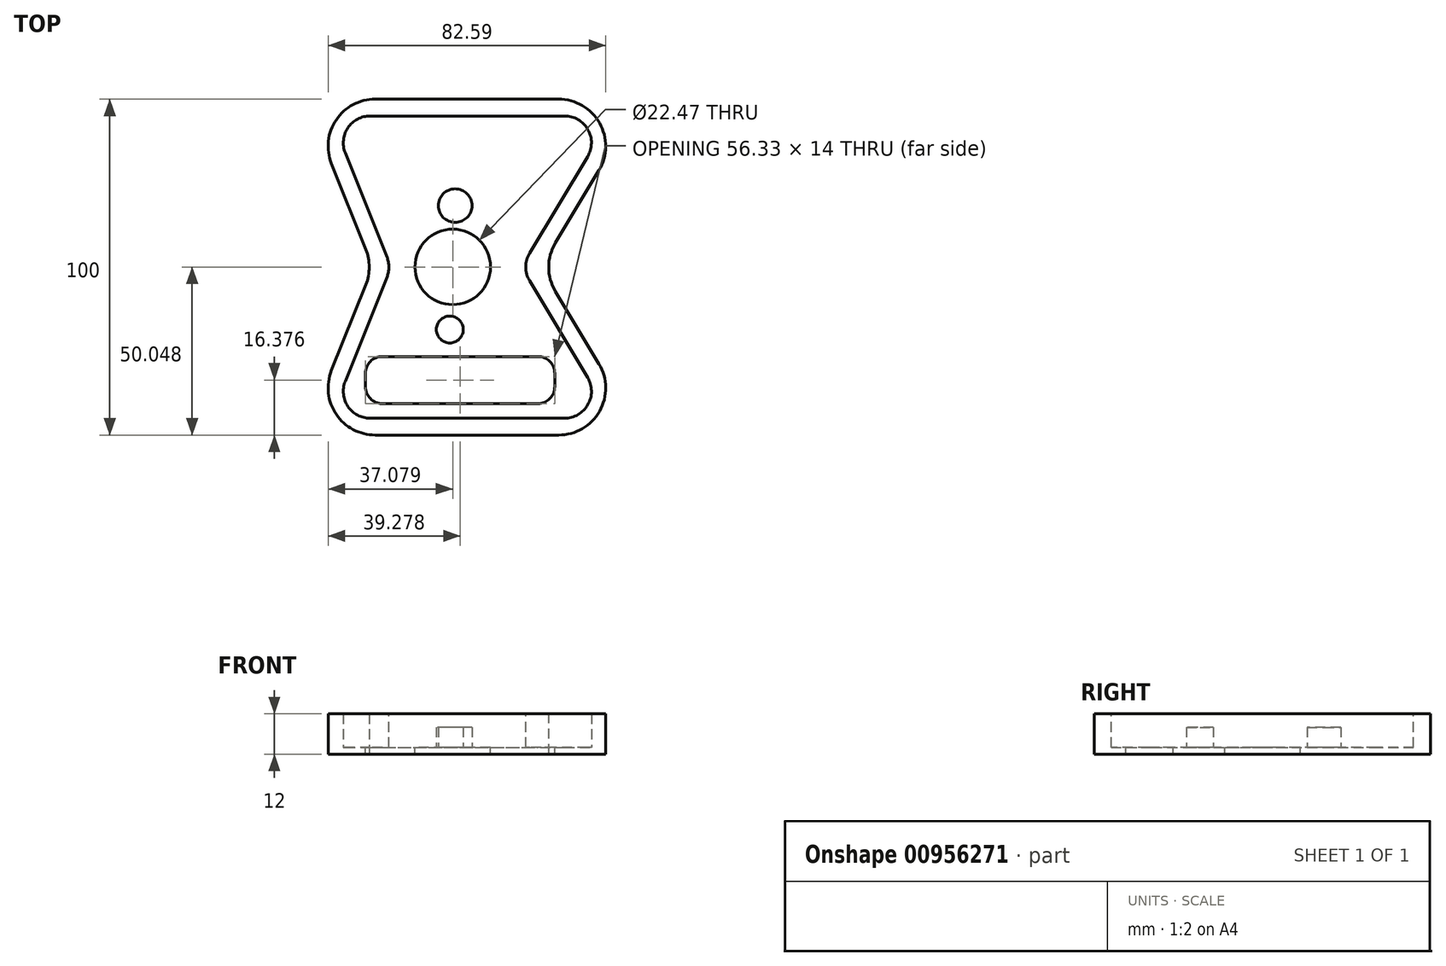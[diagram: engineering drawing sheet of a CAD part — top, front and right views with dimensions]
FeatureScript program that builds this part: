
annotation { "Feature Type Name" : "Feature", "Feature Type Description" : "" }
export const myFeature = defineFeature(function(context is Context, id is Id, definition is map)
    precondition{}
    {
        {
            var Q0;
            Q0=qCreatedBy(makeId("Top.planeOp"),FACE);
            var sketch = newSketch(context, id + "F0", { "sketchPlane" : qUnion([Q0])});
            skLineSegment(sketch, "E0.bottom", {"start": v(0, 0) * mm, "end": v(100, 0) * mm});
            skLineSegment(sketch, "E0.top", {"start": v(0, 100) * mm, "end": v(100, 100) * mm});
            skLineSegment(sketch, "E0.left", {"start": v(0, 0) * mm, "end": v(0, 100) * mm, "construction": true});
            skLineSegment(sketch, "E0.right", {"start": v(100, 0) * mm, "end": v(100, 100) * mm, "construction": true});
            skLineSegment(sketch, "E1", {"start": v(50, 0) * mm, "end": v(50, 100) * mm, "construction": true});
            skLineSegment(sketch, "E2", {"start": v(50, 50) * mm, "end": v(20, 50) * mm, "construction": true});
            skLineSegment(sketch, "E3", {"start": v(50, 50) * mm, "end": v(70, 50) * mm, "construction": true});
            skLineSegment(sketch, "E4", {"start": v(0, 100) * mm, "end": v(20, 50) * mm});
            skLineSegment(sketch, "E5", {"start": v(0, 0) * mm, "end": v(20, 50) * mm});
            skLineSegment(sketch, "E6", {"start": v(100, 0) * mm, "end": v(70, 50) * mm});
            skLineSegment(sketch, "E7", {"start": v(70, 50) * mm, "end": v(100, 100) * mm});
            skSolve(sketch);
        }
        {
            var Q0;
            Q0=makeQuery(id+"F0.imprint","IMPRINT",FACE,{"disambiguationData":[TD([[makeQuery(id+"F0.imprint","IMPRINT",EDGE,{"derivedFrom":sQuery(id+"F0.wireOp",EDGE,"E0.bottom")}),1.0]])]});
            extrude(context, id + "F1", {"entities" : qUnion([Q0]), "depth" : 12 * mm, "offsetDistance" : 25 * mm});
        }
        {
            var Q0;
            Q0=makeQuery(id+"F1.opExtrude","CAP_FACE",FACE,{"disambiguationData":[OSD([sQuery(id+"F0.wireOp",EDGE,"E0.bottom"),sQuery(id+"F0.wireOp",EDGE,"E0.top"),sQuery(id+"F0.wireOp",EDGE,"E4"),sQuery(id+"F0.wireOp",EDGE,"E5"),sQuery(id+"F0.wireOp",EDGE,"E6"),sQuery(id+"F0.wireOp",EDGE,"E7")])],"isStart":false});
            var sketch = newSketch(context, id + "F2", { "sketchPlane" : qUnion([Q0])});
            skLineSegment(sketch, "E8.0", {"start": v(64.17, 50) * mm, "end": v(91.17, 95) * mm});
            skLineSegment(sketch, "E8.1", {"start": v(7.39, 95) * mm, "end": v(25.39, 50) * mm});
            skLineSegment(sketch, "E8.2", {"start": v(25.39, 50) * mm, "end": v(7.39, 5) * mm});
            skLineSegment(sketch, "E8.3", {"start": v(91.17, 95) * mm, "end": v(7.39, 95) * mm});
            skLineSegment(sketch, "E8.4", {"start": v(7.39, 5) * mm, "end": v(91.17, 5) * mm});
            skLineSegment(sketch, "E8.5", {"start": v(91.17, 5) * mm, "end": v(64.17, 50) * mm});
            skSolve(sketch);
        }
        {
            var Q0;
            Q0=makeQuery(id+"F2.imprint","IMPRINT",FACE,{"disambiguationData":[TD([[makeQuery(id+"F2.imprint","IMPRINT",EDGE,{"derivedFrom":sQuery(id+"F2.wireOp",EDGE,"E8.0")}),1.0]])]});
            extrude(context, id + "F3", {"entities" : qUnion([Q0]), "operationType" : NewBodyOperationType.REMOVE, "oppositeDirection" : true, "depth" : 10 * mm, "offsetDistance" : 25 * mm});
        }
        {
            var Q0;
            Q0=makeQuery(id+"F3.boolean.opBoolean","COPY",FACE,{"derivedFrom":makeQuery(id+"F3.opExtrude","CAP_FACE",FACE,{"disambiguationData":[OSD([sQuery(id+"F2.wireOp",EDGE,"E8.0"),sQuery(id+"F2.wireOp",EDGE,"E8.1"),sQuery(id+"F2.wireOp",EDGE,"E8.2"),sQuery(id+"F2.wireOp",EDGE,"E8.3"),sQuery(id+"F2.wireOp",EDGE,"E8.4"),sQuery(id+"F2.wireOp",EDGE,"E8.5")])],"isStart":false})});
            var sketch = newSketch(context, id + "F4", { "sketchPlane" : qUnion([Q0])});
            skCircle(sketch, "E9", {"center": v(44.5, 68.3) * mm, "radius": 5 * mm});
            skCircle(sketch, "E10", {"center": v(42.9, 31.42) * mm, "radius": 4 * mm});
            skSolve(sketch);
        }
        {
            var Q0;
            Q0=makeQuery(id+"F4.imprint","IMPRINT",FACE,{"disambiguationData":[TD([[makeQuery(id+"F4.imprint","IMPRINT",EDGE,{"derivedFrom":sQuery(id+"F4.wireOp",EDGE,"E10")}),1.0]])]});
            var Q1;
            Q1=makeQuery(id+"F4.imprint","IMPRINT",FACE,{"disambiguationData":[TD([[makeQuery(id+"F4.imprint","IMPRINT",EDGE,{"derivedFrom":sQuery(id+"F4.wireOp",EDGE,"E9")}),1.0]])]});
            extrude(context, id + "F5", {"entities" : qUnion([Q0, Q1]), "operationType" : NewBodyOperationType.ADD, "depth" : 6 * mm, "offsetDistance" : 25 * mm});
        }
        {
            var Q0;
            Q0=makeQuery(id+"F3.boolean.opBoolean","COPY",EDGE,{"derivedFrom":makeQuery(id+"F3.opExtrude","SWEPT_EDGE",EDGE,{"disambiguationData":[OSD([sQuery(id+"F2.wireOp",EDGE,"E8.1"),sQuery(id+"F2.wireOp",EDGE,"E8.3")])]})});
            var Q1;
            Q1=makeQuery(id+"F3.boolean.opBoolean","COPY",EDGE,{"derivedFrom":makeQuery(id+"F3.opExtrude","SWEPT_EDGE",EDGE,{"disambiguationData":[OSD([sQuery(id+"F2.wireOp",EDGE,"E8.1"),sQuery(id+"F2.wireOp",EDGE,"E8.2")])]})});
            var Q2;
            Q2=makeQuery(id+"F3.boolean.opBoolean","COPY",EDGE,{"derivedFrom":makeQuery(id+"F3.opExtrude","SWEPT_EDGE",EDGE,{"disambiguationData":[OSD([sQuery(id+"F2.wireOp",EDGE,"E8.2"),sQuery(id+"F2.wireOp",EDGE,"E8.4")])]})});
            var Q3;
            Q3=makeQuery(id+"F3.boolean.opBoolean","COPY",EDGE,{"derivedFrom":makeQuery(id+"F3.opExtrude","SWEPT_EDGE",EDGE,{"disambiguationData":[OSD([sQuery(id+"F2.wireOp",EDGE,"E8.0"),sQuery(id+"F2.wireOp",EDGE,"E8.3")])]})});
            var Q4;
            Q4=makeQuery(id+"F3.boolean.opBoolean","COPY",EDGE,{"derivedFrom":makeQuery(id+"F3.opExtrude","SWEPT_EDGE",EDGE,{"disambiguationData":[OSD([sQuery(id+"F2.wireOp",EDGE,"E8.0"),sQuery(id+"F2.wireOp",EDGE,"E8.5")])]})});
            var Q5;
            Q5=makeQuery(id+"F3.boolean.opBoolean","COPY",EDGE,{"derivedFrom":makeQuery(id+"F3.opExtrude","SWEPT_EDGE",EDGE,{"disambiguationData":[OSD([sQuery(id+"F2.wireOp",EDGE,"E8.4"),sQuery(id+"F2.wireOp",EDGE,"E8.5")])]})});
            fillet(context, id + "F6", {"entities" : qUnion([Q0, Q1, Q2, Q3, Q4, Q5]), "radius" : 8 * mm, "tangentPropagation" : true, "allowEdgeOverflow" : false});
        }
        {
            var Q0;
            Q0=makeQuery(id+"F1.opExtrude","SWEPT_EDGE",EDGE,{"disambiguationData":[OSD([sQuery(id+"F0.wireOp",EDGE,"E4"),sQuery(id+"F0.wireOp",EDGE,"E5")])]});
            var Q1;
            Q1=makeQuery(id+"F1.opExtrude","SWEPT_EDGE",EDGE,{"disambiguationData":[OSD([sQuery(id+"F0.wireOp",EDGE,"E0.top"),sQuery(id+"F0.wireOp",EDGE,"E4")])]});
            var Q2;
            Q2=makeQuery(id+"F1.opExtrude","SWEPT_EDGE",EDGE,{"disambiguationData":[OSD([sQuery(id+"F0.wireOp",EDGE,"E0.top"),sQuery(id+"F0.wireOp",EDGE,"E7")])]});
            var Q3;
            Q3=makeQuery(id+"F1.opExtrude","SWEPT_EDGE",EDGE,{"disambiguationData":[OSD([sQuery(id+"F0.wireOp",EDGE,"E6"),sQuery(id+"F0.wireOp",EDGE,"E7")])]});
            var Q4;
            Q4=makeQuery(id+"F1.opExtrude","SWEPT_EDGE",EDGE,{"disambiguationData":[OSD([sQuery(id+"F0.wireOp",EDGE,"E0.bottom"),sQuery(id+"F0.wireOp",EDGE,"E6")])]});
            var Q5;
            Q5=makeQuery(id+"F1.opExtrude","SWEPT_EDGE",EDGE,{"disambiguationData":[OSD([sQuery(id+"F0.wireOp",EDGE,"E0.bottom"),sQuery(id+"F0.wireOp",EDGE,"E5")])]});
            fillet(context, id + "F7", {"entities" : qUnion([Q0, Q1, Q2, Q3, Q4, Q5]), "radius" : 14 * mm, "tangentPropagation" : true, "allowEdgeOverflow" : false});
        }
        {
            var Q0;
            Q0=makeQuery(id+"F3.boolean.opBoolean","COPY",FACE,{"derivedFrom":makeQuery(id+"F3.opExtrude","CAP_FACE",FACE,{"disambiguationData":[OSD([sQuery(id+"F2.wireOp",EDGE,"E8.0"),sQuery(id+"F2.wireOp",EDGE,"E8.1"),sQuery(id+"F2.wireOp",EDGE,"E8.2"),sQuery(id+"F2.wireOp",EDGE,"E8.3"),sQuery(id+"F2.wireOp",EDGE,"E8.4"),sQuery(id+"F2.wireOp",EDGE,"E8.5")])],"isStart":false})});
            var sketch = newSketch(context, id + "F8", { "sketchPlane" : qUnion([Q0])});
            skCircle(sketch, "E11", {"center": v(43.76, 50.05) * mm, "radius": 11.24 * mm});
            skSolve(sketch);
        }
        {
            var Q0;
            Q0=makeQuery(id+"F8.imprint","IMPRINT",FACE,{"disambiguationData":[TD([[makeQuery(id+"F8.imprint","IMPRINT",EDGE,{"derivedFrom":sQuery(id+"F8.wireOp",EDGE,"E11")}),1.0]])]});
            extrude(context, id + "F9", {"entities" : qUnion([Q0]), "operationType" : NewBodyOperationType.REMOVE, "oppositeDirection" : true, "depth" : 25 * mm, "offsetDistance" : 25 * mm});
        }
        {
            var Q0;
            Q0=makeQuery(id+"F3.boolean.opBoolean","COPY",FACE,{"derivedFrom":makeQuery(id+"F3.opExtrude","CAP_FACE",FACE,{"disambiguationData":[OSD([sQuery(id+"F2.wireOp",EDGE,"E8.0"),sQuery(id+"F2.wireOp",EDGE,"E8.1"),sQuery(id+"F2.wireOp",EDGE,"E8.2"),sQuery(id+"F2.wireOp",EDGE,"E8.3"),sQuery(id+"F2.wireOp",EDGE,"E8.4"),sQuery(id+"F2.wireOp",EDGE,"E8.5")])],"isStart":false})});
            var sketch = newSketch(context, id + "F10", { "sketchPlane" : qUnion([Q0])});
            skLineSegment(sketch, "E12.bottom", {"start": v(17.8, 23.38) * mm, "end": v(74.12, 23.38) * mm});
            skLineSegment(sketch, "E12.top", {"start": v(17.8, 9.38) * mm, "end": v(74.12, 9.38) * mm});
            skLineSegment(sketch, "E12.left", {"start": v(17.8, 23.38) * mm, "end": v(17.8, 9.38) * mm});
            skLineSegment(sketch, "E12.right", {"start": v(74.12, 23.38) * mm, "end": v(74.12, 9.38) * mm});
            skSolve(sketch);
        }
        {
            var Q0;
            Q0=makeQuery(id+"F10.imprint","IMPRINT",FACE,{"disambiguationData":[TD([[makeQuery(id+"F10.imprint","IMPRINT",EDGE,{"derivedFrom":sQuery(id+"F10.wireOp",EDGE,"E12.bottom")}),-1.0]])]});
            var sketch = newSketch(context, id + "F11", { "sketchPlane" : qUnion([Q0])});
            skSolve(sketch);
        }
        {
            var Q0;
            Q0 = qSketchRegion(id + "F11", true);
            var Q1;
            Q1=makeQuery(id+"F10.imprint","IMPRINT",FACE,{"disambiguationData":[TD([[makeQuery(id+"F10.imprint","IMPRINT",EDGE,{"derivedFrom":sQuery(id+"F10.wireOp",EDGE,"E12.bottom")}),-1.0]])]});
            extrude(context, id + "F12", {"entities" : qUnion([Q0, Q1]), "operationType" : NewBodyOperationType.REMOVE, "oppositeDirection" : true, "depth" : 25 * mm, "offsetDistance" : 25 * mm});
        }
        {
            var Q0;
            Q0=makeQuery(id+"F12.boolean.opBoolean","COPY",EDGE,{"derivedFrom":makeQuery(id+"F12.opExtrude","SWEPT_EDGE",EDGE,{"disambiguationData":[OSD([sQuery(id+"F10.wireOp",EDGE,"E12.bottom"),sQuery(id+"F10.wireOp",EDGE,"E12.left")])]})});
            var Q1;
            Q1=makeQuery(id+"F12.boolean.opBoolean","COPY",EDGE,{"derivedFrom":makeQuery(id+"F12.opExtrude","SWEPT_EDGE",EDGE,{"disambiguationData":[OSD([sQuery(id+"F10.wireOp",EDGE,"E12.bottom"),sQuery(id+"F10.wireOp",EDGE,"E12.right")])]})});
            var Q2;
            Q2=makeQuery(id+"F12.boolean.opBoolean","COPY",EDGE,{"derivedFrom":makeQuery(id+"F12.opExtrude","SWEPT_EDGE",EDGE,{"disambiguationData":[OSD([sQuery(id+"F10.wireOp",EDGE,"E12.top"),sQuery(id+"F10.wireOp",EDGE,"E12.right")])]})});
            var Q3;
            Q3=makeQuery(id+"F12.boolean.opBoolean","COPY",EDGE,{"derivedFrom":makeQuery(id+"F12.opExtrude","SWEPT_EDGE",EDGE,{"disambiguationData":[OSD([sQuery(id+"F10.wireOp",EDGE,"E12.top"),sQuery(id+"F10.wireOp",EDGE,"E12.left")])]})});
            fillet(context, id + "F13", {"entities" : qUnion([Q0, Q1, Q2, Q3]), "radius" : 5 * mm, "tangentPropagation" : true, "allowEdgeOverflow" : false});
        }
    });
